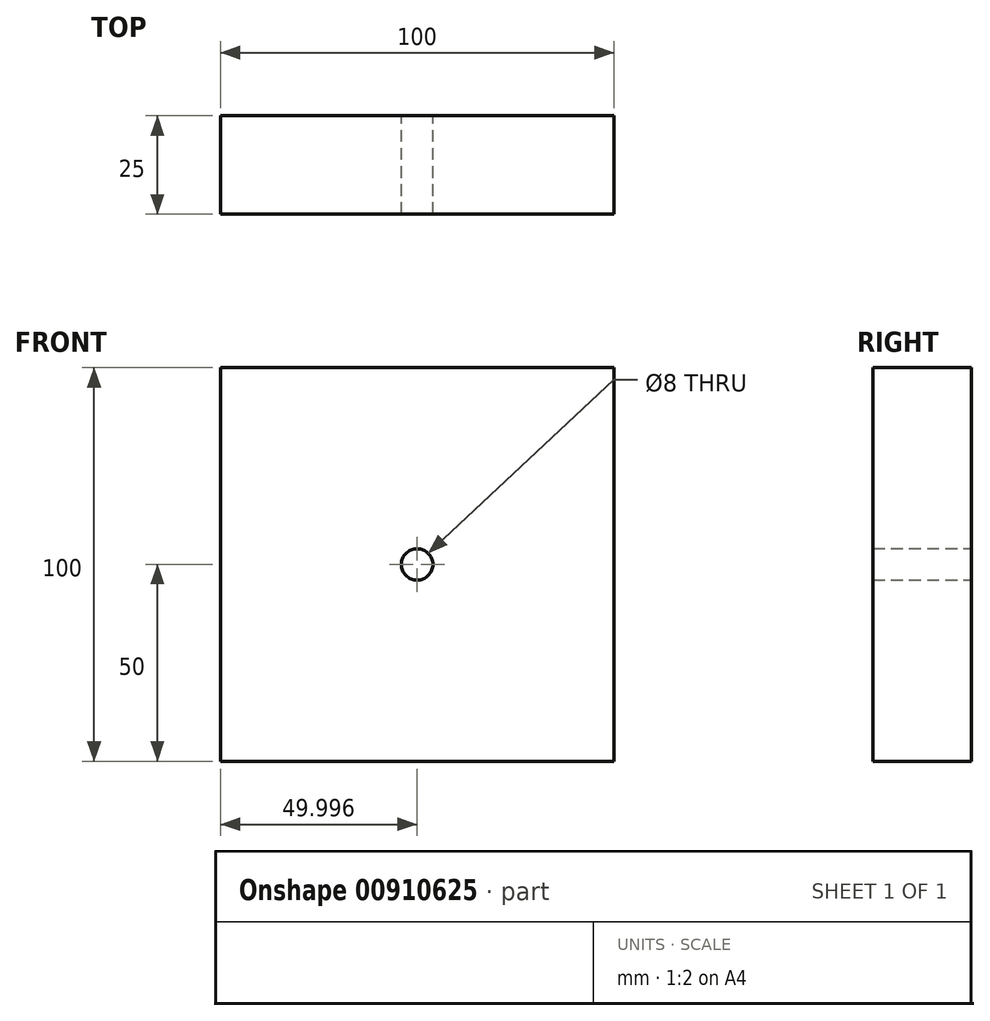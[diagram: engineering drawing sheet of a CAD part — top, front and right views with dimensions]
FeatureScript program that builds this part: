
annotation { "Feature Type Name" : "Feature", "Feature Type Description" : "" }
export const myFeature = defineFeature(function(context is Context, id is Id, definition is map)
    precondition{}
    {
        {
            var Q0;
            Q0=qCreatedBy(makeId("Front.planeOp"),FACE);
            var sketch = newSketch(context, id + "F0", { "sketchPlane" : qUnion([Q0])});
            skLineSegment(sketch, "E0.bottom", {"start": v(-58.2, 59.9) * mm, "end": v(41.8, 59.9) * mm});
            skLineSegment(sketch, "E0.top", {"start": v(-58.2, -40.1) * mm, "end": v(41.8, -40.1) * mm});
            skLineSegment(sketch, "E0.left", {"start": v(-58.2, 59.9) * mm, "end": v(-58.2, -40.1) * mm});
            skLineSegment(sketch, "E0.right", {"start": v(41.8, 59.9) * mm, "end": v(41.8, -40.1) * mm});
            skCircle(sketch, "E1", {"center": v(-8.2, 9.9) * mm, "radius": 4 * mm});
            skPoint(sketch, "E2.start.orphan", {"position": v(-8.2, 59.9) * mm});
            skSolve(sketch);
        }
        {
            var Q0;
            Q0 = qSketchRegion(id + "F0", true);
            extrude(context, id + "F1", {"entities" : qUnion([Q0]), "depth" : 25 * mm, "offsetDistance" : 25 * mm});
        }
    });
